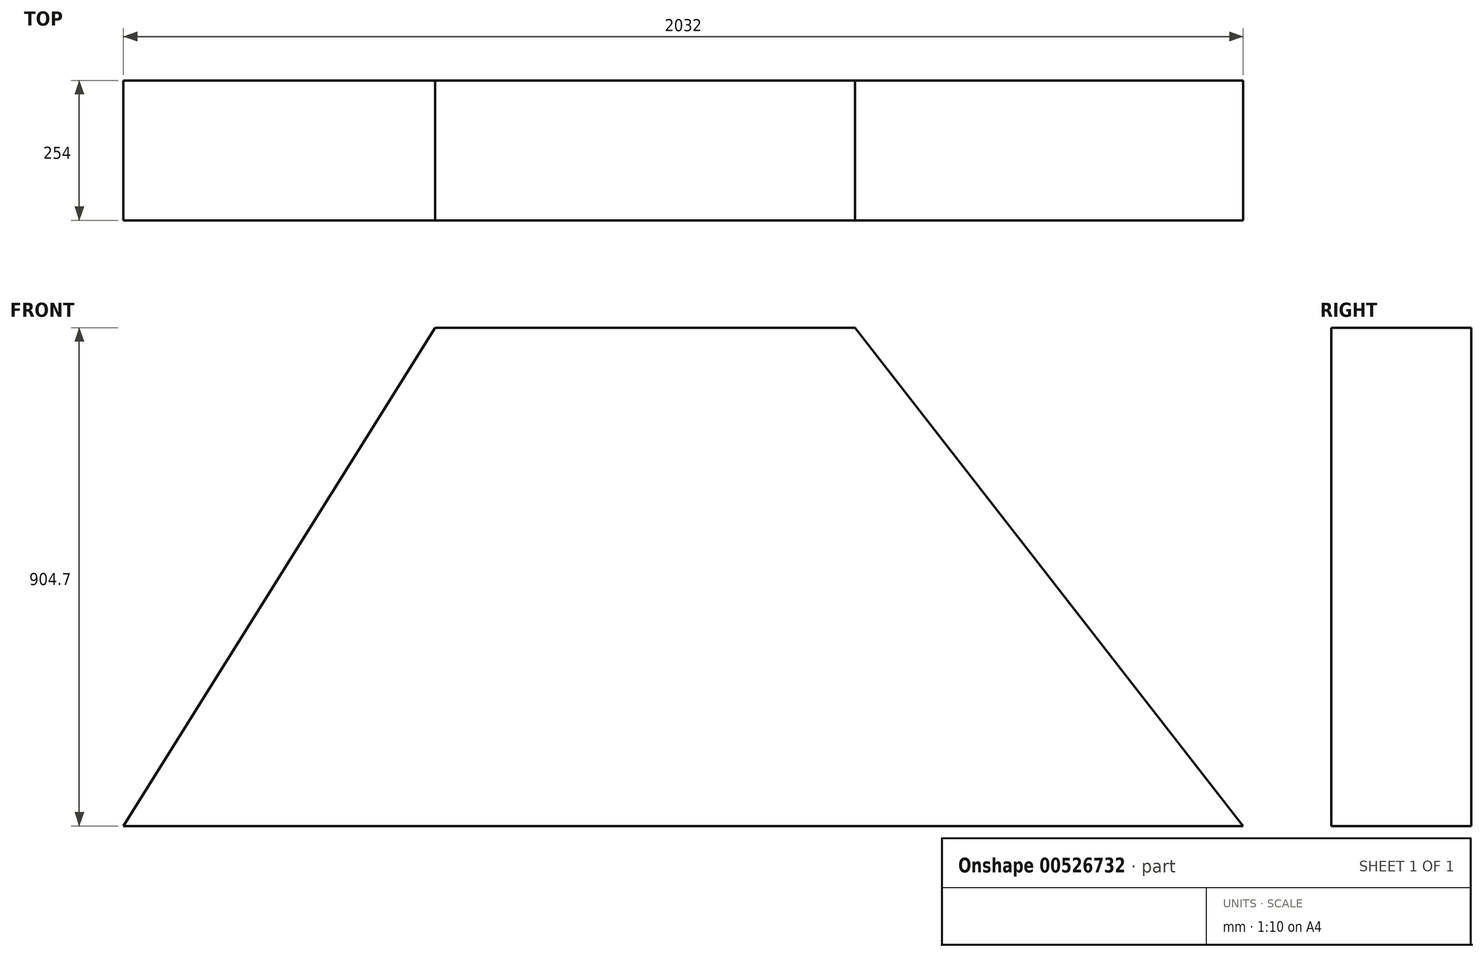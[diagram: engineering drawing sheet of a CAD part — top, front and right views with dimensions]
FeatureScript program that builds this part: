
annotation { "Feature Type Name" : "Feature", "Feature Type Description" : "" }
export const myFeature = defineFeature(function(context is Context, id is Id, definition is map)
    precondition{}
    {
        {
            var Q0;
            Q0=qCreatedBy(makeId("Front.planeOp"),FACE);
            var sketch = newSketch(context, id + "F0", { "sketchPlane" : qUnion([Q0])});
            skLineSegment(sketch, "E0", {"start": v(0, 0) * mm, "end": v(2032, 0) * mm});
            skLineSegment(sketch, "E1", {"start": v(0, 0) * mm, "end": v(565.32, 904.7) * mm});
            skLineSegment(sketch, "E2", {"start": v(565.32, 904.7) * mm, "end": v(1327.32, 904.7) * mm});
            skLineSegment(sketch, "E3", {"start": v(1327.32, 904.7) * mm, "end": v(2032, 0) * mm});
            skSolve(sketch);
        }
        {
            var Q0;
            Q0 = qSketchRegion(id + "F0", true);
            extrude(context, id + "F1", {"entities" : qUnion([Q0]), "depth" : 254 * mm, "offsetDistance" : 25.4 * mm});
        }
    });
